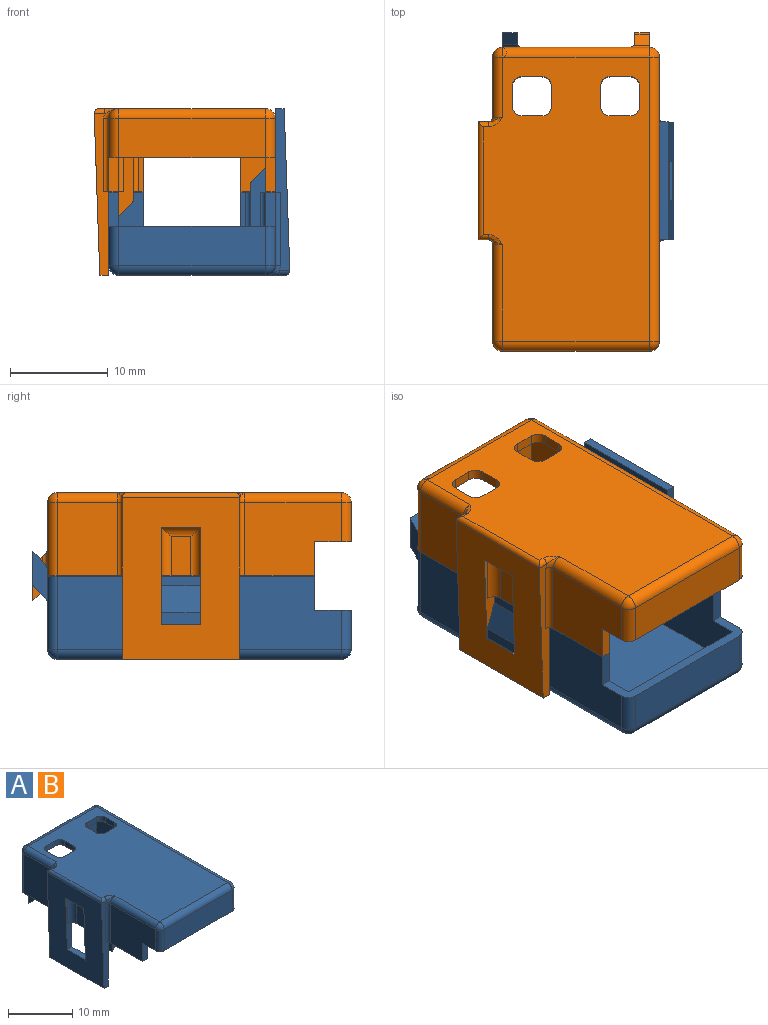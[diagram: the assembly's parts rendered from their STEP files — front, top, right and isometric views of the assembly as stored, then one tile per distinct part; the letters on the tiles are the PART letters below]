
ASSEMBLY  parts=2 mates=1
PART A: 108 faces, bbox 20x33x18.5 mm
  f0: plane 29.54x17.52mm, normal (0,0,1), area 427.4mm2, adj f52,f54,f57,f59,f73,f74,f75,f76
  f1: plane 30x15mm, normal (0,0,-1), area 406mm2, adj f3,f8,f12,f13,f14,f19,f35,f36
  f2: plane 7.5x4.5mm, normal (0,1,0), area 14.2mm2, adj f7,f21,f53,f57,f64,f65,f71
  f3: plane 14.5x7.5mm, normal (1,0,0), area 108.7mm2, adj f1,f17,f66,f69
  f4: plane 29x7.5mm, normal (1,0,0), area 192.7mm2, adj f7,f9,f18,f30,f31,f32,f51,f53
  f5: plane 4x2mm, normal (-1,0,0), area 8mm2, adj f17,f105,f106,f107
  f6: plane 7.5x6.13mm, normal (-1,0,0), area 45.9mm2, adj f17,f56,f59,f96
  f7: plane 27.75x3.5mm, normal (0,0,-1), area 29.6mm2, adj f2,f4,f14,f18,f19,f21,f42,f43
  f8: plane 7.5x2.5mm, normal (0,-1,0), area 4.6mm2, adj f1,f17,f20,f68,f70
  f9: plane 17x3.75mm, normal (0,0,-1), area 22.1mm2, adj f4,f10,f11,f12,f13,f14,f16,f18
  f10: plane 9.88x7.5mm, normal (-1,0,0), area 64.4mm2, adj f9,f16,f17,f91,f93,f104
  f11: plane 15x4mm, normal (0,-1,0), area 60mm2, adj f9,f52,f91,f94
  f12: plane 15x4mm, normal (0,1,0), area 60mm2, adj f1,f9,f13,f14
  f13: plane 10x7.5mm, normal (1,0,0), area 65.4mm2, adj f1,f9,f12,f16,f17,f67
  f14: plane 29x7.5mm, normal (-1,0,0), area 207.9mm2, adj f1,f7,f9,f12,f18,f19
  f15: plane 7.5x4.5mm, normal (0,1,0), area 19.6mm2, adj f17,f20,f56,f57,f70
  f16: plane 3.5x1mm, normal (0,-1,0), area 3.5mm2, adj f9,f10,f13,f17
  f17: plane 27.25x4.5mm, normal (0,0,-1), area 30.3mm2, adj f3,f5,f6,f8,f10,f13,f15,f16
  f18: plane 3.5x1mm, normal (0,-1,0), area 3.5mm2, adj f4,f7,f9,f14
  f19: plane 7.5x4.5mm, normal (0,-1,0), area 19.6mm2, adj f1,f7,f14,f21,f71
  f20: plane 5.5x1mm, normal (1,0,0), area 5.5mm2, adj f8,f15,f17,f70
  f21: plane 5.5x1mm, normal (-1,0,0), area 5.5mm2, adj f2,f7,f19,f71
  f22: plane 16.5x1.48mm, normal (0,-1,0), area 15.7mm2, adj f17,f28,f29,f72,f100,f101,f103,f104
  f23: plane 16.5x1.48mm, normal (0,1,0), area 15.7mm2, adj f17,f28,f29,f72,f96,f97,f99,f100
  f24: plane 4x0.38mm, normal (0,0,-1), area 1.5mm2, adj f25,f27,f72,f106
  f25: plane 10x1.38mm, normal (0,1,0), area 7mm2, adj f17,f24,f26,f29,f72,f105
  f26: plane 4x1.03mm, normal (0,0,1), area 4.1mm2, adj f25,f27,f29,f72
  f27: plane 10x1.38mm, normal (0,-1,0), area 7mm2, adj f17,f24,f26,f29,f72,f107
  f28: plane 12x0.91mm, normal (0,0,-1), area 10.9mm2, adj f22,f23,f29,f72
  f29: plane 12x8.5mm, normal (1,0,0), area 82mm2, adj f17,f22,f23,f25,f26,f27,f28
  f30: plane 3.9x1mm, normal (0,0,1), area 3.9mm2, adj f4,f31,f32,f33
  f31: plane 3.9x1mm, normal (0,-1,0), area 2.5mm2, adj f4,f30,f33,f51
  f32: plane 3.9x1mm, normal (0,1,0), area 2.5mm2, adj f4,f30,f33,f51
  f33: plane 3.9x1.15mm, normal (1,0,0), area 4.5mm2, adj f30,f31,f32,f51
  f34: plane 2.5x1.5mm, normal (0,1,0), area 2.6mm2, adj f17,f35,f37,f48,f62
  f35: plane 8.29x1.5mm, normal (1,0,0), area 8.7mm2, adj f1,f17,f34,f36,f62,f68
  f36: plane 8.29x1.5mm, normal (0,-1,0), area 8.7mm2, adj f1,f17,f35,f37,f61,f69
  f37: plane 2.5x1.5mm, normal (-1,0,0), area 2.6mm2, adj f17,f34,f36,f49,f61
  f38: plane 2.5x1.5mm, normal (-1,0,0), area 3.7mm2, adj f17,f39,f41,f47
  f39: plane 10x1.5mm, normal (0,1,0), area 10.1mm2, adj f1,f17,f38,f40,f47,f63,f66
  f40: plane 8.29x1.5mm, normal (1,0,0), area 12.4mm2, adj f1,f39,f41,f63
  f41: plane 10x1.5mm, normal (0,-1,0), area 10.1mm2, adj f1,f17,f38,f40,f47,f63,f67
  f42: plane 1.5x0.59mm, normal (0,-1,0), area 0.9mm2, adj f7,f43,f45,f90
  f43: plane 4.5x1.5mm, normal (-1,0,0), area 4.1mm2, adj f7,f42,f44,f46,f50,f60,f64,f89
  f44: plane 3.29x1.5mm, normal (0,1,0), area 4.9mm2, adj f43,f45,f46,f60
  f45: plane 5.21x1.5mm, normal (1,0,0), area 5.2mm2, adj f42,f44,f46,f50,f53,f60,f65,f89
  f46: plane 1.5x0mm, normal (0,0,-1), area 0mm2, adj f43,f44,f45,f89
  f47: plane 1.5x1.35mm, normal (0.71,0,-0.71), area 2.9mm2, adj f38,f39,f41,f63
  f48: plane 1.35x1.35mm, normal (0.71,0,-0.71), area 1.3mm2, adj f34,f49,f62
  f49: plane 1.35x1.35mm, normal (0,-0.71,-0.71), area 1.3mm2, adj f37,f48,f61
  f50: plane 1.68x1.24mm, normal (0,0.71,0.71), area 2.6mm2, adj f43,f45,f60,f64,f65
  f51: plane 3.9x2.75mm, normal (0.94,0,-0.34), area 11.4mm2, adj f4,f31,f32,f33
  f52: cylinder r=1mm len=15mm, axis (1,0,0), area 23.6mm2, adj f0,f11,f92,f95
  f53: cylinder r=1mm len=7.5mm, axis (0,0,-1), area 11.8mm2, adj f2,f4,f7,f45,f55
  f54: cylinder r=1mm len=29mm, axis (0,-1,0), area 45.6mm2, adj f0,f4,f55,f95
  f55: sphere r=1mm, area 1mm2, adj f53,f54,f57
  f56: cylinder r=1mm len=7.5mm, axis (0,0,1), area 11.8mm2, adj f6,f15,f17,f58
  f57: cylinder r=1mm len=15mm, axis (1,0,0), area 23.6mm2, adj f0,f1,f2,f15,f55,f58
  f58: sphere r=1mm, area 2.1mm2, adj f56,f57,f59
  f59: cylinder r=1mm len=6.13mm, axis (0,1,0), area 9.6mm2, adj f0,f6,f58,f97
  f60: cylinder r=0.5mm len=1.5mm, axis (1,0,0), area 0.6mm2, adj f43,f44,f45,f50
  f61: cylinder r=0.5mm len=1.5mm, axis (-1,0,0), area 0.6mm2, adj f36,f37,f49,f62
  f62: cylinder r=0.5mm len=1.5mm, axis (0,-1,0), area 0.6mm2, adj f34,f35,f48,f61
  f63: cylinder r=0.5mm len=1.5mm, axis (0,-1,0), area 0.6mm2, adj f39,f40,f41,f47
  f64: cylinder r=0.5mm len=2.71mm, axis (0,0,1), area 1.8mm2, adj f2,f7,f43,f50,f65
  f65: cylinder r=0.5mm len=2mm, axis (1,0,0), area 0.7mm2, adj f2,f45,f50,f64
  f66: cylinder r=0.5mm len=7.5mm, axis (0,0,-1), area 5.9mm2, adj f1,f3,f17,f39
  f67: cylinder r=0.5mm len=7.5mm, axis (0,0,1), area 5.9mm2, adj f1,f13,f17,f41
  f68: cylinder r=0.5mm len=7.5mm, axis (0,0,1), area 5.9mm2, adj f1,f8,f17,f35
  f69: cylinder r=0.5mm len=7.5mm, axis (0,0,1), area 5.9mm2, adj f1,f3,f17,f36
  f70: cylinder r=2mm len=2mm, axis (0,-1,0), area 3.1mm2, adj f1,f8,f15,f20
  f71: cylinder r=2mm len=2mm, axis (0,1,0), area 3.1mm2, adj f1,f2,f19,f21
  f72: plane 16.48x12mm, normal (-1,0,-0.03), area 157.9mm2, adj f22,f23,f24,f25,f26,f27,f28,f100
  f73: plane 2x1mm, normal (0,-1,0), area 2mm2, adj f0,f1,f81,f84
  f74: plane 2x1mm, normal (1,0,0), area 2mm2, adj f0,f1,f81,f82
  f75: plane 2x1mm, normal (0,1,0), area 2mm2, adj f0,f1,f82,f83
  f76: plane 2x1mm, normal (-1,0,0), area 2mm2, adj f0,f1,f83,f84
  f77: plane 2x1mm, normal (-1,0,0), area 2mm2, adj f0,f1,f85,f86
  f78: plane 2x1mm, normal (0,-1,0), area 2mm2, adj f0,f1,f86,f88
  f79: plane 2x1mm, normal (1,0,0), area 2mm2, adj f0,f1,f87,f88
  f80: plane 2x1mm, normal (0,1,0), area 2mm2, adj f0,f1,f85,f87
  f81: cylinder r=1mm len=1mm, axis (0,0,1), area 1.6mm2, adj f0,f1,f73,f74
  f82: cylinder r=1mm len=1mm, axis (0,0,-1), area 1.6mm2, adj f0,f1,f74,f75
  f83: cylinder r=1mm len=1mm, axis (0,0,1), area 1.6mm2, adj f0,f1,f75,f76
  f84: cylinder r=1mm len=1mm, axis (0,0,-1), area 1.6mm2, adj f0,f1,f73,f76
  f85: cylinder r=1mm len=1mm, axis (0,0,1), area 1.6mm2, adj f0,f1,f77,f80
  f86: cylinder r=1mm len=1mm, axis (0,0,-1), area 1.6mm2, adj f0,f1,f77,f78
  f87: cylinder r=1mm len=1mm, axis (0,0,-1), area 1.6mm2, adj f0,f1,f79,f80
  f88: cylinder r=1mm len=1mm, axis (0,0,1), area 1.6mm2, adj f0,f1,f78,f79
  f89: plane 1.5x1.21mm, normal (0,-0.71,-0.71), area 2.6mm2, adj f43,f45,f46,f90
  f90: cylinder r=1mm len=1.5mm, axis (-1,0,0), area 1.2mm2, adj f42,f43,f45,f89
  f91: cylinder r=1mm len=4mm, axis (0,0,1), area 6.3mm2, adj f9,f10,f11,f92
  f92: sphere r=1mm, area 1.6mm2, adj f52,f91,f93
  f93: cylinder r=1mm len=9.88mm, axis (0,1,0), area 15.5mm2, adj f0,f10,f92,f103
  f94: cylinder r=1mm len=4mm, axis (0,0,-1), area 6.3mm2, adj f4,f9,f11,f95
  f95: sphere r=1mm, area 1.6mm2, adj f52,f54,f94
  f96: cylinder r=0.5mm len=7.5mm, axis (0,0,1), area 5.9mm2, adj f6,f17,f23,f97
  f97: torus R=1.5mm, axis (0,-1,0), area 0.7mm2, adj f23,f59,f96,f98
  f98: bspline ~1.41x1mm, area 0.5mm2, adj f0,f97,f99
  f99: cylinder r=0.5mm len=1.07mm, axis (1,0,0), area 0.6mm2, adj f0,f23,f98,f100
  f100: cylinder r=0.5mm len=12mm, axis (0,-1,0), area 9.3mm2, adj f0,f22,f23,f72,f99,f101
  f101: cylinder r=0.5mm len=1.07mm, axis (-1,0,0), area 0.6mm2, adj f0,f22,f100,f102
  f102: bspline ~1.67x1mm, area 0.4mm2, adj f0,f101,f103
  f103: torus R=1.5mm, axis (0,-1,0), area 0.7mm2, adj f22,f93,f102,f104
  f104: cylinder r=0.5mm len=7.5mm, axis (0,0,-1), area 5.9mm2, adj f10,f17,f22,f103
  f105: cylinder r=1mm len=5mm, axis (0,0,1), area 7.1mm2, adj f5,f17,f25,f106
  f106: cylinder r=1mm len=4mm, axis (0,1,0), area 4.7mm2, adj f5,f24,f105,f107
  f107: cylinder r=1mm len=5mm, axis (0,0,-1), area 7.1mm2, adj f5,f17,f27,f106
PART B: same geometry as A
PLACE A rot(axis=(0,1,0),180deg) t=(-46.72,-29.69,13.01)mm
PLACE B t=(-46.72,-29.69,25.01)mm
MATE fastened A.f7 <-> B.f17  axis (0,0,1) through (-54.72,-26.94,19.01)mm
